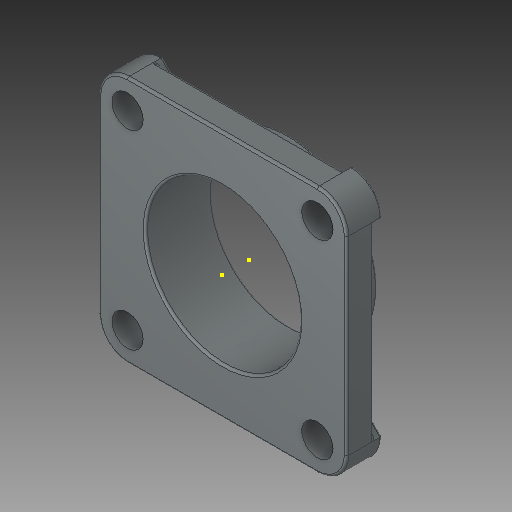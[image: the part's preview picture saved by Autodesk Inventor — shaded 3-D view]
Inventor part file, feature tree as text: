
AUTODESK INVENTOR PART (.ipt)
format: ipt  version: 2019 (Build 230136000, 136)  size: 445,440 bytes
history: native  units: in
note: dims shown in document units (in); Inventor stores cm internally (conversion verified against a paired STEP export)
features: sketch x10, other x3
ambient origin geometry x8: Origin, YZ Plane, XZ Plane, XY Plane, X Axis, Y Axis, Z Axis, Center Point
bodies: Solid1 (feature_tree)
feature tree (13):
  other  "project flange bearing part1.ipt"
  other  "Solid1::project flange bearing part1.ipt"
  other  "TaggingFeature1"
  sketch  "Sketch1"  dims[d0=0.3937in]
  sketch  "Sketch2"
  sketch  "Sketch3"
  sketch  "Sketch4"
  sketch  "Sketch5"
  sketch  "Sketch6"
  sketch  "Sketch7"
  sketch  "Sketch8"
  sketch  "Sketch9"
  sketch  "Sketch10"
